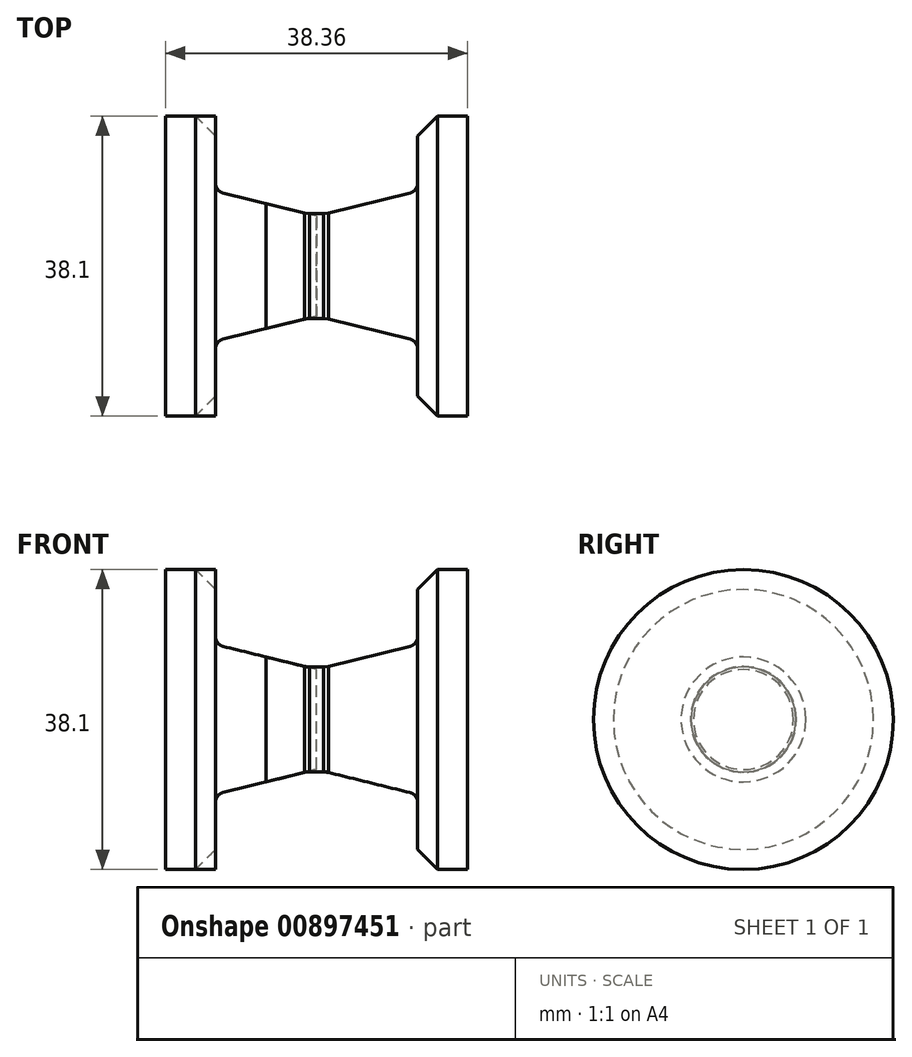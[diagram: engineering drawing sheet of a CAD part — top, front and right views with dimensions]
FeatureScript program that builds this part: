
annotation { "Feature Type Name" : "Feature", "Feature Type Description" : "" }
export const myFeature = defineFeature(function(context is Context, id is Id, definition is map)
    precondition{}
    {
        {
            var Q0;
            Q0=qCreatedBy(makeId("Top.planeOp"),FACE);
            var sketch = newSketch(context, id + "F0", { "sketchPlane" : qUnion([Q0])});
            skLineSegment(sketch, "E0.bottom", {"start": v(0, 6.35) * mm, "end": v(-19.18, 6.35) * mm});
            skLineSegment(sketch, "E0.top", {"start": v(0, 0) * mm, "end": v(-19.18, 0) * mm});
            skLineSegment(sketch, "E0.left", {"start": v(0, 6.35) * mm, "end": v(0, 0) * mm});
            skLineSegment(sketch, "E0.right", {"start": v(-19.18, 6.35) * mm, "end": v(-19.18, 0) * mm});
            skLineSegment(sketch, "E1.bottom", {"start": v(-19.18, 0) * mm, "end": v(-12.83, 0) * mm});
            skLineSegment(sketch, "E1.top", {"start": v(-19.18, 12.7) * mm, "end": v(-12.83, 12.7) * mm});
            skLineSegment(sketch, "E1.left", {"start": v(-19.18, 0) * mm, "end": v(-19.18, 12.7) * mm});
            skLineSegment(sketch, "E1.right", {"start": v(-12.83, 0) * mm, "end": v(-12.83, 12.7) * mm});
            skLineSegment(sketch, "E2.MirrorCS", {"start": v(0, 6.35) * mm, "end": v(19.18, 6.35) * mm});
            skLineSegment(sketch, "E3.MirrorCS", {"start": v(12.83, 0) * mm, "end": v(12.83, 12.7) * mm});
            skLineSegment(sketch, "E4.MirrorCS", {"start": v(19.18, 12.7) * mm, "end": v(12.83, 12.7) * mm});
            skLineSegment(sketch, "E5.MirrorCS", {"start": v(19.18, 0) * mm, "end": v(19.18, 12.7) * mm});
            skLineSegment(sketch, "E6.MirrorCS", {"start": v(0, 0) * mm, "end": v(19.18, 0) * mm});
            skLineSegment(sketch, "E7.bottom", {"start": v(-12.83, 12.7) * mm, "end": v(-19.18, 12.7) * mm});
            skLineSegment(sketch, "E7.top", {"start": v(-12.83, 19.05) * mm, "end": v(-19.18, 19.05) * mm});
            skLineSegment(sketch, "E7.left", {"start": v(-12.83, 12.7) * mm, "end": v(-12.83, 19.05) * mm});
            skLineSegment(sketch, "E7.right", {"start": v(-19.18, 12.7) * mm, "end": v(-19.18, 19.05) * mm});
            skLineSegment(sketch, "E8", {"start": v(-12.83, 6.35) * mm, "end": v(-12.83, 12.7) * mm});
            skLineSegment(sketch, "E9", {"start": v(-12.83, 9.53) * mm, "end": v(0, 6.35) * mm});
            skLineSegment(sketch, "E10", {"start": v(0, 6.35) * mm, "end": v(12.83, 9.53) * mm});
            skLineSegment(sketch, "E11.MirrorCS", {"start": v(12.83, 12.7) * mm, "end": v(12.83, 19.05) * mm});
            skLineSegment(sketch, "E12.MirrorCS", {"start": v(12.83, 19.05) * mm, "end": v(19.18, 19.05) * mm});
            skLineSegment(sketch, "E13.MirrorCS", {"start": v(19.18, 12.7) * mm, "end": v(19.18, 19.05) * mm});
            skLineSegment(sketch, "E14.top", {"start": v(-6.41, 0) * mm, "end": v(0, 0) * mm});
            skLineSegment(sketch, "E14.left", {"start": v(-6.41, 7.94) * mm, "end": v(-6.41, 0) * mm});
            skSolve(sketch);
        }
        {
            var Q0;
            {var subQ4=sQuery(id+"F0.wireOp",EDGE,"E1.top");Q0=makeQuery(id+"F0.imprint","IMPRINT",FACE,{"disambiguationData":[TD([[makeQuery(id+"F0.imprint","IMPRINT",EDGE,{"derivedFrom":subQ4}),-1.0]])]});}
            var Q1;
            {var subQ0=sQuery(id+"F0.wireOp",EDGE,"E0.right");Q1=makeQuery(id+"F0.imprint","IMPRINT",FACE,{"disambiguationData":[TD([[makeQuery(id+"F0.imprint","IMPRINT",EDGE,{"derivedFrom":subQ0}),1.0]])]});}
            var Q2;
            {var subQ0=sQuery(id+"F0.wireOp",EDGE,"E0.left");Q2=makeQuery(id+"F0.imprint","IMPRINT",FACE,{"disambiguationData":[TD([[makeQuery(id+"F0.imprint","IMPRINT",EDGE,{"derivedFrom":subQ0}),-1.0]])]});}
            var Q3;
            {var subQ0=sQuery(id+"F0.wireOp",EDGE,"E0.left");Q3=makeQuery(id+"F0.imprint","IMPRINT",FACE,{"disambiguationData":[TD([[makeQuery(id+"F0.imprint","IMPRINT",EDGE,{"derivedFrom":subQ0}),1.0]])]});}
            var Q4;
            {var subQ0=sQuery(id+"F0.wireOp",EDGE,"E5.MirrorCS");var subQ1=sQuery(id+"F0.wireOp",EDGE,"E2.MirrorCS");var subQ2=makeQuery(id+"F0.imprint","INTERSECT",VERTEX,{"derivedFrom":[subQ1,subQ0]});Q4=makeQuery(id+"F0.imprint","IMPRINT",FACE,{"disambiguationData":[TD([[makeQuery(id+"F0.imprint","IMPRINT",EDGE,{"disambiguationData":[TD([[subQ2,1.0]])],"derivedFrom":subQ1}),-1.0]])]});}
            var Q5;
            {var subQ5=sQuery(id+"F0.wireOp",EDGE,"E4.MirrorCS");Q5=makeQuery(id+"F0.imprint","IMPRINT",FACE,{"disambiguationData":[TD([[makeQuery(id+"F0.imprint","IMPRINT",EDGE,{"derivedFrom":subQ5}),1.0]])]});}
            var Q6;
            Q6=makeQuery(id+"F0.imprint","IMPRINT",FACE,{"disambiguationData":[TD([[makeQuery(id+"F0.imprint","IMPRINT",EDGE,{"derivedFrom":sQuery(id+"F0.wireOp",EDGE,"E4.MirrorCS")}),-1.0]])]});
            var Q7;
            {var subQ0=sQuery(id+"F0.wireOp",EDGE,"E10");Q7=makeQuery(id+"F0.imprint","IMPRINT",FACE,{"disambiguationData":[TD([[makeQuery(id+"F0.imprint","IMPRINT",EDGE,{"derivedFrom":subQ0}),-1.0]])]});}
            var Q8;
            {var subQ0=sQuery(id+"F0.wireOp",EDGE,"E9");Q8=makeQuery(id+"F0.imprint","IMPRINT",FACE,{"disambiguationData":[TD([[makeQuery(id+"F0.imprint","IMPRINT",EDGE,{"derivedFrom":subQ0}),-1.0]])]});}
            var Q9;
            Q9=makeQuery(id+"F0.imprint","IMPRINT",FACE,{"disambiguationData":[TD([[makeQuery(id+"F0.imprint","IMPRINT",EDGE,{"derivedFrom":sQuery(id+"F0.wireOp",EDGE,"E1.top")}),1.0]])]});
            var Q10;
            {var subQ0=sQuery(id+"F0.wireOp",EDGE,"E14.left");var subQ1=sQuery(id+"F0.wireOp",EDGE,"E0.bottom");var subQ2=makeQuery(id+"F0.imprint","INTERSECT",VERTEX,{"derivedFrom":[subQ1,subQ0]});Q10=makeQuery(id+"F0.imprint","IMPRINT",FACE,{"disambiguationData":[TD([[makeQuery(id+"F0.imprint","IMPRINT",EDGE,{"disambiguationData":[TD([[subQ2,-1.0]])],"derivedFrom":subQ1}),1.0]])]});}
            var Q11;
            {var subQ0=sQuery(id+"F0.wireOp",EDGE,"E14.left");var subQ1=sQuery(id+"F0.wireOp",EDGE,"E0.bottom");var subQ2=makeQuery(id+"F0.imprint","INTERSECT",VERTEX,{"derivedFrom":[subQ1,subQ0]});Q11=makeQuery(id+"F0.imprint","IMPRINT",FACE,{"disambiguationData":[TD([[makeQuery(id+"F0.imprint","IMPRINT",EDGE,{"disambiguationData":[TD([[subQ2,-1.0]])],"derivedFrom":subQ1}),-1.0]])]});}
            var Q12;
            Q12=sQuery(id+"F0.wireOp",EDGE,"E0.top");
            revolve(context, id + "F1", {"surfaceOperationType" : NewSurfaceOperationType.NEW, "entities" : qUnion([Q0, Q1, Q2, Q3, Q4, Q5, Q6, Q7, Q8, Q9, Q10, Q11]), "axis" : qUnion([Q12]), "revolveType" : RevolveType.FULL});
        }
        {
            var Q0;
            Q0=makeQuery(id+"F1.opRevolve","SWEPT_EDGE",EDGE,{"disambiguationData":[OSD([sQuery(id+"F0.wireOp",EDGE,"E0.bottom"),sQuery(id+"F0.wireOp",EDGE,"E1.right")])]});
            var Q1;
            Q1=makeQuery(id+"F1.opRevolve","SWEPT_EDGE",EDGE,{"disambiguationData":[OSD([sQuery(id+"F0.wireOp",EDGE,"E2.MirrorCS"),sQuery(id+"F0.wireOp",EDGE,"E3.MirrorCS")])]});
            fillet(context, id + "F2", {"entities" : qUnion([Q0, Q1]), "tangentPropagation" : true, "radius" : 1.27 * mm, "defaultsChanged" : true, "vertexSettings" : [], "allowEdgeOverflow" : false});
        }
        {
            var Q0;
            Q0=makeQuery(id+"F1.opRevolve","SWEPT_EDGE",EDGE,{"disambiguationData":[OSD([sQuery(id+"F0.wireOp",EDGE,"E0.bottom"),sQuery(id+"F0.wireOp",EDGE,"E0.left"),sQuery(id+"F0.wireOp",EDGE,"E2.MirrorCS"),sQuery(id+"F0.wireOp",EDGE,"E9"),sQuery(id+"F0.wireOp",EDGE,"E10")])]});
            chamfer(context, id + "F3", {"entities" : qUnion([Q0]), "width" : 5.08 * mm, "tangentPropagation" : true});
        }
        {
            var Q0;
            Q0=makeQuery(id+"F1.opRevolve","SWEPT_EDGE",EDGE,{"disambiguationData":[OSD([sQuery(id+"F0.wireOp",EDGE,"E7.top"),sQuery(id+"F0.wireOp",EDGE,"E7.left")])]});
            var Q1;
            Q1=makeQuery(id+"F1.opRevolve","SWEPT_EDGE",EDGE,{"disambiguationData":[OSD([sQuery(id+"F0.wireOp",EDGE,"E11.MirrorCS"),sQuery(id+"F0.wireOp",EDGE,"E12.MirrorCS")])]});
            chamfer(context, id + "F4", {"entities" : qUnion([Q0, Q1]), "width" : 2.54 * mm, "tangentPropagation" : true});
        }
        {
            var Q0;
            {var subQ0=sQuery(id+"F0.wireOp",EDGE,"E9");Q0=makeQuery(id+"F3.opChamfer","BLEND_EDGE",EDGE,{"blendedFrom":[makeQuery(id+"F1.opRevolve","SWEPT_EDGE",EDGE,{"disambiguationData":[OSD([sQuery(id+"F0.wireOp",EDGE,"E0.bottom"),sQuery(id+"F0.wireOp",EDGE,"E0.left"),sQuery(id+"F0.wireOp",EDGE,"E2.MirrorCS"),subQ0,sQuery(id+"F0.wireOp",EDGE,"E10")])]}),makeQuery(id+"F1.opRevolve","SWEPT_FACE",FACE,{"disambiguationData":[OSD([subQ0])]})],"blendedInto":[makeQuery(id+"F1.opRevolve","SWEPT_FACE",FACE,{"disambiguationData":[OSD([subQ0])]})]});}
            var Q1;
            {var subQ0=sQuery(id+"F0.wireOp",EDGE,"E10");Q1=makeQuery(id+"F3.opChamfer","BLEND_EDGE",EDGE,{"blendedFrom":[makeQuery(id+"F1.opRevolve","SWEPT_EDGE",EDGE,{"disambiguationData":[OSD([sQuery(id+"F0.wireOp",EDGE,"E0.bottom"),sQuery(id+"F0.wireOp",EDGE,"E0.left"),sQuery(id+"F0.wireOp",EDGE,"E2.MirrorCS"),sQuery(id+"F0.wireOp",EDGE,"E9"),subQ0])]}),makeQuery(id+"F1.opRevolve","SWEPT_FACE",FACE,{"disambiguationData":[OSD([subQ0])]})],"blendedInto":[makeQuery(id+"F1.opRevolve","SWEPT_FACE",FACE,{"disambiguationData":[OSD([subQ0])]})]});}
            chamfer(context, id + "F5", {"entities" : qUnion([Q0, Q1]), "width" : 2.54 * mm, "tangentPropagation" : true});
        }
        {
            var Q0;
            {var subQ0=sQuery(id+"F0.wireOp",EDGE,"E0.right");Q0=makeQuery(id+"F0.imprint","IMPRINT",FACE,{"disambiguationData":[TD([[makeQuery(id+"F0.imprint","IMPRINT",EDGE,{"derivedFrom":subQ0}),1.0]])]});}
            var Q1;
            {var subQ5=sQuery(id+"F0.wireOp",EDGE,"E1.top");Q1=makeQuery(id+"F0.imprint","IMPRINT",FACE,{"disambiguationData":[TD([[makeQuery(id+"F0.imprint","IMPRINT",EDGE,{"derivedFrom":subQ5}),-1.0]])]});}
            var Q2;
            Q2=makeQuery(id+"F0.imprint","IMPRINT",FACE,{"disambiguationData":[TD([[makeQuery(id+"F0.imprint","IMPRINT",EDGE,{"derivedFrom":sQuery(id+"F0.wireOp",EDGE,"E1.top")}),1.0]])]});
            var Q3;
            {var subQ0=sQuery(id+"F0.wireOp",EDGE,"E9");Q3=makeQuery(id+"F0.imprint","IMPRINT",FACE,{"disambiguationData":[TD([[makeQuery(id+"F0.imprint","IMPRINT",EDGE,{"derivedFrom":subQ0}),-1.0]])]});}
            var Q4;
            {var subQ0=sQuery(id+"F0.wireOp",EDGE,"E0.left");Q4=makeQuery(id+"F0.imprint","IMPRINT",FACE,{"disambiguationData":[TD([[makeQuery(id+"F0.imprint","IMPRINT",EDGE,{"derivedFrom":subQ0}),-1.0]])]});}
            var Q5;
            Q5=sQuery(id+"F0.wireOp",EDGE,"E0.top");
            revolve(context, id + "F6", {"surfaceOperationType" : NewSurfaceOperationType.NEW, "entities" : qUnion([Q0, Q1, Q2, Q3, Q4]), "axis" : qUnion([Q5]), "revolveType" : RevolveType.FULL});
        }
    });
